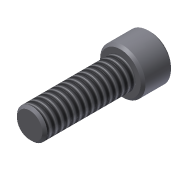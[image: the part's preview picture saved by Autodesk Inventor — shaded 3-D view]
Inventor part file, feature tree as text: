
AUTODESK INVENTOR PART (.ipt)
format: ipt  version: 2011 SP1 (Build 150282100, 282)  size: 109,568 bytes
history: native  units: in
note: dims shown in document units (in); Inventor stores cm internally (conversion verified against a paired STEP export)
features: extrude x3, sketch x3, chamfer x1, thread x1
ambient origin geometry x8: Origin, YZ Plane, XZ Plane, XY Plane, X Axis, Y Axis, Z Axis, Center Point
bodies: Solid1 (feature_tree)
feature tree (8):
  extrude  "Extrusion1"  Depth=0.75in TaperAngle=0.0deg
  extrude  "Extrusion2"  Depth=0.25in TaperAngle=0.0deg
  extrude  "Extrusion3"  Depth=0.125in TaperAngle=0.0deg
  chamfer  "Chamfer1"  Distance=0.02in Angle=45.0deg
  thread  "Thread1"  [1 undecoded]
  sketch  "Sketch1"  dims[d0=0.25in d1=0.75in d2=0.0in]
  sketch  "Sketch2"  dims[d3=0.375in d4=0.25in d5=0.0in]
  sketch  "Sketch3"  dims[d6=0.1875in d7=0.125in d8=0.0in d9=0.02in d10=0.125in d11=45.0deg d12=1.0in d13=0.0in]
note: 1 required parameter value undecoded (feature->parameter linkage not recoverable at this tier; creation-order binding heuristic only, values carry confidence <= 0.55)
